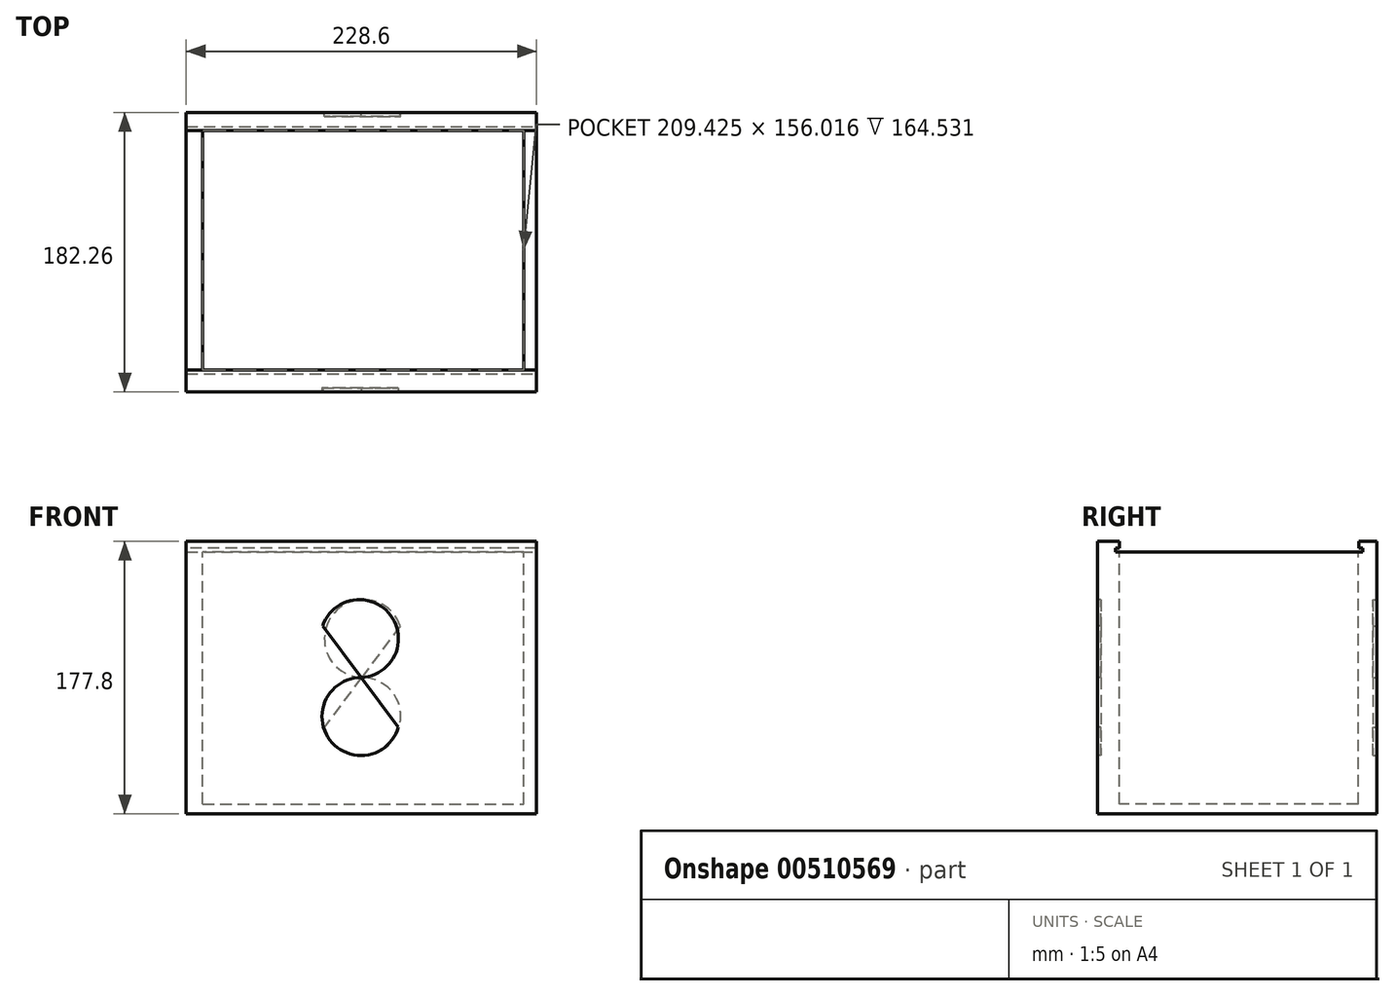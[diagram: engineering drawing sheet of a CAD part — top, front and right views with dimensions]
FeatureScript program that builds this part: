
annotation { "Feature Type Name" : "Feature", "Feature Type Description" : "" }
export const myFeature = defineFeature(function(context is Context, id is Id, definition is map)
    precondition{}
    {
        {
            var Q0;
            Q0=qCreatedBy(makeId("Top.planeOp"),FACE);
            var sketch = newSketch(context, id + "F0", { "sketchPlane" : qUnion([Q0])});
            skLineSegment(sketch, "E0", {"start": v(0, 0) * mm, "end": v(114.3, 0) * mm});
            skLineSegment(sketch, "E1", {"start": v(0, 0) * mm, "end": v(-114.3, 0) * mm});
            skLineSegment(sketch, "E2", {"start": v(114.3, 0) * mm, "end": v(114.3, 182.26) * mm});
            skLineSegment(sketch, "E3", {"start": v(114.3, 182.26) * mm, "end": v(-114.3, 182.26) * mm});
            skLineSegment(sketch, "E4", {"start": v(-114.3, 182.26) * mm, "end": v(-114.3, 0) * mm});
            skSolve(sketch);
        }
        {
            var Q0;
            Q0 = qSketchRegion(id + "F0", true);
            extrude(context, id + "F1", {"entities" : qUnion([Q0]), "depth" : 177.8 * mm});
        }
        {
            var Q0;
            Q0=makeQuery(id+"F1.opExtrude","CAP_FACE",FACE,{"disambiguationData":[OSD([sQuery(id+"F0.wireOp",EDGE,"E0"),sQuery(id+"F0.wireOp",EDGE,"E1"),sQuery(id+"F0.wireOp",EDGE,"E2"),sQuery(id+"F0.wireOp",EDGE,"E3"),sQuery(id+"F0.wireOp",EDGE,"E4")])],"isStart":false});
            var sketch = newSketch(context, id + "F2", { "sketchPlane" : qUnion([Q0])});
            skLineSegment(sketch, "E5.bottom", {"start": v(-103.6, 170.38) * mm, "end": v(105.83, 170.38) * mm});
            skLineSegment(sketch, "E5.top", {"start": v(-103.6, 14.37) * mm, "end": v(105.83, 14.37) * mm});
            skLineSegment(sketch, "E5.left", {"start": v(-103.6, 170.38) * mm, "end": v(-103.6, 14.37) * mm});
            skLineSegment(sketch, "E5.right", {"start": v(105.83, 170.38) * mm, "end": v(105.83, 14.37) * mm});
            skSolve(sketch);
        }
        {
            var Q0;
            Q0 = qSketchRegion(id + "F2", true);
            extrude(context, id + "F3", {"entities" : qUnion([Q0]), "operationType" : NewBodyOperationType.REMOVE, "oppositeDirection" : true, "depth" : 171.45 * mm});
        }
        {
            var Q0;
            Q0=makeQuery(id+"F1.opExtrude","SWEPT_FACE",FACE,{"disambiguationData":[OSD([sQuery(id+"F0.wireOp",EDGE,"E2")])]});
            var sketch = newSketch(context, id + "F4", { "sketchPlane" : qUnion([Q0])});
            skLineSegment(sketch, "E6.bottom", {"start": v(14.98, 177.8) * mm, "end": v(170.54, 177.8) * mm});
            skLineSegment(sketch, "E6.top", {"start": v(14.98, 170.88) * mm, "end": v(170.54, 170.88) * mm});
            skLineSegment(sketch, "E6.left", {"start": v(14.98, 177.8) * mm, "end": v(14.98, 170.88) * mm});
            skLineSegment(sketch, "E6.right", {"start": v(170.54, 177.8) * mm, "end": v(170.54, 170.88) * mm});
            skSolve(sketch);
        }
        {
            var Q0;
            Q0 = qSketchRegion(id + "F4", true);
            extrude(context, id + "F5", {"entities" : qUnion([Q0]), "operationType" : NewBodyOperationType.REMOVE, "endBound" : BoundingType.THROUGH_ALL, "oppositeDirection" : true, "depth" : 25.4 * mm});
        }
        {
            var Q0;
            Q0=makeQuery(id+"F1.opExtrude","SWEPT_FACE",FACE,{"disambiguationData":[OSD([sQuery(id+"F0.wireOp",EDGE,"E2")])]});
            var sketch = newSketch(context, id + "F6", { "sketchPlane" : qUnion([Q0])});
            skLineSegment(sketch, "E7.bottom", {"start": v(170.54, 170.88) * mm, "end": v(173.08, 170.88) * mm});
            skLineSegment(sketch, "E7.top", {"start": v(170.54, 173.42) * mm, "end": v(173.08, 173.42) * mm});
            skLineSegment(sketch, "E7.left", {"start": v(170.54, 170.88) * mm, "end": v(170.54, 173.42) * mm});
            skLineSegment(sketch, "E7.right", {"start": v(173.08, 170.88) * mm, "end": v(173.08, 173.42) * mm});
            skSolve(sketch);
        }
        {
            var Q0;
            Q0 = qSketchRegion(id + "F6", true);
            extrude(context, id + "F7", {"entities" : qUnion([Q0]), "operationType" : NewBodyOperationType.REMOVE, "endBound" : BoundingType.THROUGH_ALL, "oppositeDirection" : true, "depth" : 25.4 * mm});
        }
        {
            var Q0;
            Q0=makeQuery(id+"F1.opExtrude","SWEPT_FACE",FACE,{"disambiguationData":[OSD([sQuery(id+"F0.wireOp",EDGE,"E2")])]});
            var sketch = newSketch(context, id + "F8", { "sketchPlane" : qUnion([Q0])});
            skLineSegment(sketch, "E8.bottom", {"start": v(14.98, 170.88) * mm, "end": v(12.44, 170.88) * mm});
            skLineSegment(sketch, "E8.top", {"start": v(14.98, 173.42) * mm, "end": v(12.44, 173.42) * mm});
            skLineSegment(sketch, "E8.left", {"start": v(14.98, 170.88) * mm, "end": v(14.98, 173.42) * mm});
            skLineSegment(sketch, "E8.right", {"start": v(12.44, 170.88) * mm, "end": v(12.44, 173.42) * mm});
            skSolve(sketch);
        }
        {
            var Q0;
            Q0 = qSketchRegion(id + "F8", true);
            extrude(context, id + "F9", {"entities" : qUnion([Q0]), "operationType" : NewBodyOperationType.REMOVE, "endBound" : BoundingType.THROUGH_ALL, "oppositeDirection" : true, "depth" : 25.4 * mm});
        }
        {
            var Q0;
            {var subQ0=sQuery(id+"F0.wireOp",EDGE,"E2");var subQ1=sQuery(id+"F0.wireOp",EDGE,"E4");var subQ2=sQuery(id+"F0.wireOp",EDGE,"E1");var subQ3=sQuery(id+"F0.wireOp",EDGE,"E0");Q0=makeQuery(id+"F5.boolean.opBoolean","SPLIT",FACE,{"disambiguationData":[TD([makeQuery(id+"F3.boolean.opBoolean","COPY",FACE,{"derivedFrom":makeQuery(id+"F3.opExtrude","SWEPT_FACE",FACE,{"disambiguationData":[OSD([sQuery(id+"F2.wireOp",EDGE,"E5.top")])]})})])],"derivedFrom":makeQuery(id+"F1.opExtrude","CAP_FACE",FACE,{"disambiguationData":[OSD([subQ3,subQ2,subQ0,sQuery(id+"F0.wireOp",EDGE,"E3"),subQ1])],"isStart":false})});}
            var sketch = newSketch(context, id + "F10", { "sketchPlane" : qUnion([Q0])});
            skLineSegment(sketch, "E9", {"start": v(105.83, 14.37) * mm, "end": v(114.3, 14.37) * mm});
            skLineSegment(sketch, "E10", {"start": v(114.3, 14.37) * mm, "end": v(114.3, 14.98) * mm});
            skLineSegment(sketch, "E11", {"start": v(114.3, 14.98) * mm, "end": v(105.83, 14.98) * mm});
            skLineSegment(sketch, "E12", {"start": v(105.83, 14.98) * mm, "end": v(105.83, 14.37) * mm});
            skSolve(sketch);
        }
        {
            var Q0;
            Q0 = qSketchRegion(id + "F10", true);
            extrude(context, id + "F11", {"entities" : qUnion([Q0]), "operationType" : NewBodyOperationType.REMOVE, "oppositeDirection" : true, "depth" : 5.08 * mm});
        }
        {
            var Q0;
            {var subQ0=sQuery(id+"F0.wireOp",EDGE,"E2");var subQ1=sQuery(id+"F0.wireOp",EDGE,"E4");var subQ2=sQuery(id+"F0.wireOp",EDGE,"E1");var subQ3=sQuery(id+"F0.wireOp",EDGE,"E0");Q0=makeQuery(id+"F5.boolean.opBoolean","SPLIT",FACE,{"disambiguationData":[TD([makeQuery(id+"F3.boolean.opBoolean","COPY",FACE,{"derivedFrom":makeQuery(id+"F3.opExtrude","SWEPT_FACE",FACE,{"disambiguationData":[OSD([sQuery(id+"F2.wireOp",EDGE,"E5.top")])]})})])],"derivedFrom":makeQuery(id+"F1.opExtrude","CAP_FACE",FACE,{"disambiguationData":[OSD([subQ3,subQ2,subQ0,sQuery(id+"F0.wireOp",EDGE,"E3"),subQ1])],"isStart":false})});}
            var sketch = newSketch(context, id + "F12", { "sketchPlane" : qUnion([Q0])});
            skLineSegment(sketch, "E13.bottom", {"start": v(-103.6, 14.37) * mm, "end": v(-114.3, 14.37) * mm});
            skLineSegment(sketch, "E13.top", {"start": v(-103.6, 14.98) * mm, "end": v(-114.3, 14.98) * mm});
            skLineSegment(sketch, "E13.left", {"start": v(-103.6, 14.37) * mm, "end": v(-103.6, 14.98) * mm});
            skLineSegment(sketch, "E13.right", {"start": v(-114.3, 14.37) * mm, "end": v(-114.3, 14.98) * mm});
            skSolve(sketch);
        }
        {
            var Q0;
            Q0 = qSketchRegion(id + "F12", true);
            extrude(context, id + "F13", {"entities" : qUnion([Q0]), "operationType" : NewBodyOperationType.REMOVE, "oppositeDirection" : true, "depth" : 5.08 * mm});
        }
        {
            var Q0;
            Q0=makeQuery(id+"F1.opExtrude","SWEPT_FACE",FACE,{"disambiguationData":[OSD([sQuery(id+"F0.wireOp",EDGE,"E2")])]});
            var sketch = newSketch(context, id + "F14", { "sketchPlane" : qUnion([Q0])});
            skLineSegment(sketch, "E14", {"start": v(14.37, 173.42) * mm, "end": v(11.83, 173.42) * mm});
            skLineSegment(sketch, "E15", {"start": v(11.83, 173.42) * mm, "end": v(11.83, 170.88) * mm});
            skLineSegment(sketch, "E16", {"start": v(11.83, 170.88) * mm, "end": v(12.44, 170.88) * mm});
            skLineSegment(sketch, "E17", {"start": v(12.44, 173.42) * mm, "end": v(12.44, 170.88) * mm});
            skSolve(sketch);
        }
        {
            var Q0;
            Q0 = qSketchRegion(id + "F14", true);
            extrude(context, id + "F15", {"entities" : qUnion([Q0]), "operationType" : NewBodyOperationType.REMOVE, "endBound" : BoundingType.THROUGH_ALL, "oppositeDirection" : true, "depth" : 25.4 * mm});
        }
        {
            var Q0;
            Q0=makeQuery(id+"F1.opExtrude","SWEPT_FACE",FACE,{"disambiguationData":[OSD([sQuery(id+"F0.wireOp",EDGE,"E2")])]});
            var sketch = newSketch(context, id + "F16", { "sketchPlane" : qUnion([Q0])});
            skSolve(sketch);
        }
        {
            var Q0;
            Q0=makeQuery(id+"F1.opExtrude","SWEPT_FACE",FACE,{"disambiguationData":[OSD([sQuery(id+"F0.wireOp",EDGE,"E0"),sQuery(id+"F0.wireOp",EDGE,"E1")])]});
            var sketch = newSketch(context, id + "F17", { "sketchPlane" : qUnion([Q0])});
            skLineSegment(sketch, "E18", {"start": v(-114.3, 88.9) * mm, "end": v(114.3, 88.9) * mm, "construction": true});
            skLineSegment(sketch, "E19.bottom", {"start": v(0, 38.1) * mm, "end": v(-0.62, 38.1) * mm});
            skLineSegment(sketch, "E19.top", {"start": v(0.17, 139.7) * mm, "end": v(-2.73, 139.7) * mm});
            skPoint(sketch, "E19.middle", {"position": v(0, 88.9) * mm});
            skLineSegment(sketch, "E20", {"start": v(-25.31, 122.65) * mm, "end": v(24.16, 56.69) * mm});
            skArc(sketch, "E21", {"start": v(-0.23, 88.9) * mm, "mid": v(-0.03, 88.9) * mm, "end": v(0.17, 88.9) * mm});
            skArc(sketch, "E22", {"start": v(0, 88.9) * mm, "mid": v(-20.63, 48.26) * mm, "end": v(24.16, 56.69) * mm});
            skPoint(sketch, "E23.end.orphan", {"position": v(0, 38.1) * mm});
            skPoint(sketch, "E24.1.internal.orphan", {"position": v(0, 139.7) * mm});
            skArc(sketch, "E25.trimOffspring", {"start": v(0.17, 139.7) * mm, "mid": v(0.08, 139.7) * mm, "end": v(0, 139.7) * mm});
            skArc(sketch, "E26", {"start": v(-2.73, 88.9) * mm, "mid": v(19.86, 128.45) * mm, "end": v(-25.31, 122.65) * mm});
            skPoint(sketch, "E26.third.point", {"position": v(24.16, 114.3) * mm});
            skPoint(sketch, "E27.orphan", {"position": v(-38.1, 139.7) * mm});
            skPoint(sketch, "E28.orphan", {"position": v(38.1, 139.7) * mm});
            skPoint(sketch, "E29.orphan", {"position": v(38.1, 38.1) * mm});
            skPoint(sketch, "E30.orphan", {"position": v(-38.1, 38.1) * mm});
            skSolve(sketch);
        }
        {
            var Q0;
            Q0 = qSketchRegion(id + "F17", true);
            extrude(context, id + "F18", {"entities" : qUnion([Q0]), "operationType" : NewBodyOperationType.REMOVE, "oppositeDirection" : true, "depth" : 2.54 * mm, "offsetDistance" : 25.4 * mm});
        }
        {
            var Q0;
            Q0=makeQuery(id+"F1.opExtrude","SWEPT_FACE",FACE,{"disambiguationData":[OSD([sQuery(id+"F0.wireOp",EDGE,"E3")])]});
            var sketch = newSketch(context, id + "F19", { "sketchPlane" : qUnion([Q0])});
            skLineSegment(sketch, "E31", {"start": v(114.3, 88.9) * mm, "end": v(-114.3, 88.9) * mm, "construction": true});
            skLineSegment(sketch, "E32", {"start": v(0, 177.8) * mm, "end": v(0, 0) * mm, "construction": true});
            skLineSegment(sketch, "E33", {"start": v(-114.3, 88.9) * mm, "end": v(114.3, 88.9) * mm, "construction": true});
            skLineSegment(sketch, "E34.bottom", {"start": v(0, 38.1) * mm, "end": v(-0.62, 38.1) * mm});
            skLineSegment(sketch, "E34.top", {"start": v(0.17, 139.7) * mm, "end": v(-2.73, 139.7) * mm});
            skPoint(sketch, "E34.middle", {"position": v(0, 88.9) * mm});
            skLineSegment(sketch, "E35", {"start": v(-25.31, 122.65) * mm, "end": v(24.16, 56.69) * mm});
            skArc(sketch, "E36", {"start": v(-0.23, 88.9) * mm, "mid": v(-0.03, 88.9) * mm, "end": v(0.17, 88.9) * mm});
            skArc(sketch, "E37", {"start": v(0, 88.9) * mm, "mid": v(-20.63, 48.26) * mm, "end": v(24.16, 56.69) * mm});
            skPoint(sketch, "E38.end.orphan", {"position": v(0, 38.1) * mm});
            skPoint(sketch, "E39.1.internal.orphan", {"position": v(0, 139.7) * mm});
            skArc(sketch, "E40.trimOffspring", {"start": v(0.17, 139.7) * mm, "mid": v(0.08, 139.7) * mm, "end": v(0, 139.7) * mm});
            skArc(sketch, "E41", {"start": v(-2.73, 88.9) * mm, "mid": v(19.86, 128.45) * mm, "end": v(-25.31, 122.65) * mm});
            skPoint(sketch, "E41.third.point", {"position": v(24.16, 114.3) * mm});
            skPoint(sketch, "E42.orphan", {"position": v(-38.1, 139.7) * mm});
            skPoint(sketch, "E43.orphan", {"position": v(38.1, 139.7) * mm});
            skPoint(sketch, "E44.orphan", {"position": v(38.1, 38.1) * mm});
            skPoint(sketch, "E45.orphan", {"position": v(-38.1, 38.1) * mm});
            skSolve(sketch);
        }
        {
            var Q0;
            Q0 = qSketchRegion(id + "F19", true);
            extrude(context, id + "F20", {"entities" : qUnion([Q0]), "operationType" : NewBodyOperationType.REMOVE, "oppositeDirection" : true, "depth" : 2.54 * mm, "offsetDistance" : 25.4 * mm});
        }
    });
